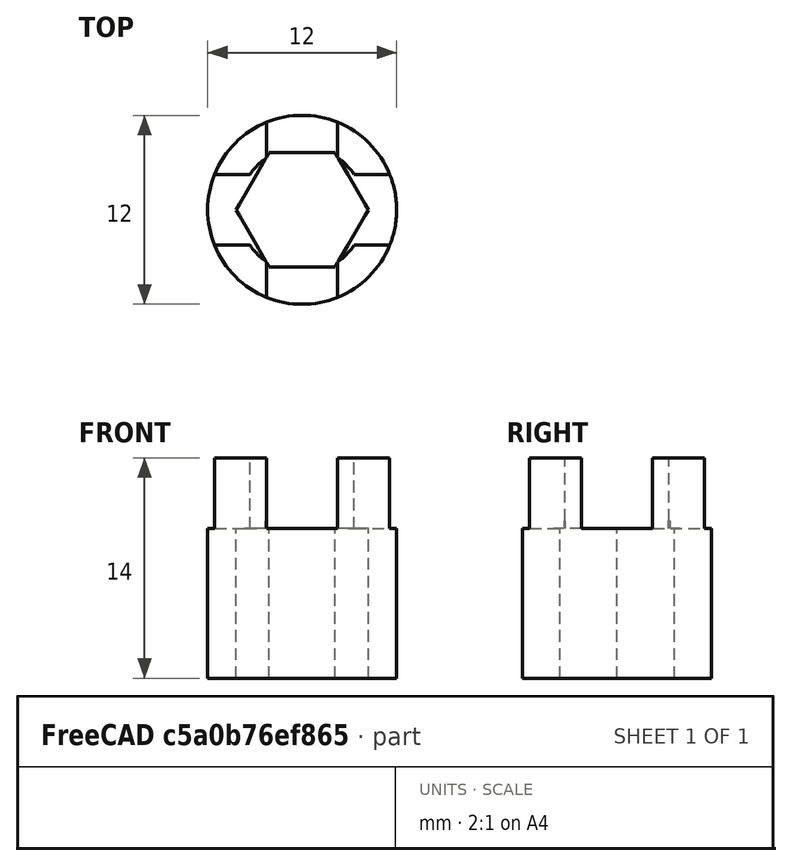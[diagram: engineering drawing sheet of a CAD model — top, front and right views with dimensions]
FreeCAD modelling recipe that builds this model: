
FCSTD DOCUMENT  (FreeCAD 0.19R23634 (Git))
Label: Stage-Nut
License: All rights reserved
LicenseURL: http://en.wikipedia.org/wiki/All_rights_reserved
objects: Part::Box×2, Part::Cylinder×2, Part::Prism×1, Part::MultiFuse×1, Part::Cut×1, PartDesign::FeatureBase×1, PartDesign::CoordinateSystem×1, PartDesign::Body×1, App::Part×1
note: 10 computed .brp shape members not serialized (recipe doc carries the construction recipe); baked Part::Feature solids carry a one-line shape summary decoded from their .brp

FEATURE [Part::Box] cube029
  AttacherType = Attacher::AttachEngine3D
  Height = 4.5
  Length = 4.5
  Placement = pos=(-69.15,-76.9,-7) rot=(0,0,1;0rad)
  Width = 20
FEATURE [Part::Cylinder] cylinder019
  Angle = 360
  AttacherType = Attacher::AttachEngine3D
  Height = 4.5
  Placement = pos=(-66.9,-66.9,-7) rot=(0,0,1;0rad)
  Radius = 4
FEATURE [Part::Prism] prism022
  AttacherType = Attacher::AttachEngine3D
  Circumradius = 4.2
  FirstAngle = 0
  Height = 10
  Placement = pos=(-66.9,-66.9,-16.5) rot=(0,0,1;0rad)
  Polygon = 6
  SecondAngle = 0
FEATURE [Part::Cylinder] cylinder018
  Angle = 360
  AttacherType = Attacher::AttachEngine3D
  Height = 14
  Placement = pos=(-66.9,-66.9,-16.5) rot=(0,0,1;0rad)
  Radius = 6
FEATURE [Part::Box] cube028
  AttacherType = Attacher::AttachEngine3D
  Height = 4.5
  Length = 20
  Placement = pos=(-76.9,-69.15,-7) rot=(0,0,1;0rad)
  Width = 4.5
FEATURE [Part::MultiFuse] Group012
  Shapes = -> [prism022,cylinder019,cube028,cube029]
FEATURE [Part::Cut] difference007
  Base = -> cylinder018
  Tool = -> Group012
FEATURE [PartDesign::FeatureBase] BaseFeature007
  BaseFeature = -> difference007
FEATURE [PartDesign::CoordinateSystem] LCS_0
  AttacherType = Attacher::AttachEngine3D
  MapMode = 45
  Placement = pos=(-66.9,-66.9,-16.5) rot=(0,0,1;0rad)
  Support = -> [BaseFeature007]
FEATURE [PartDesign::Body] Body007  label="Nut001"
  BaseFeature = -> difference007
  Group = -> [BaseFeature007]
  Origin = -> Origin007
  Tip = -> BaseFeature007
FEATURE [App::Part] Nut
  Group = -> [LCS_0,cube028,cube029,Group012,cylinder019,cylinder018,difference007,prism022,Body007]
  Origin = -> Origin
